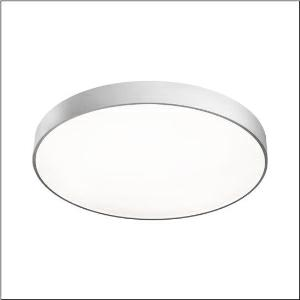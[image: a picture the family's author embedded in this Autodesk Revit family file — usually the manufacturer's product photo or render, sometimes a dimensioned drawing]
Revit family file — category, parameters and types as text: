
# Revit family: round_21_l_51mr38fd0421s
name_source: partatom
category: Lighting Fixtures
units: mm (PartAtom-declared; Revit-internal decimal feet)

## family parameters
Cut with Voids When Loaded = No
Host = Face
Light Source = No
Part Type = Normal
Room Calculation Point = No
Round Connector Dimension = Use Diameter
Shared = No

## types (1)
- Round 21 L (1 x LED, 13080 lm, 98.3 W, 4000K)
    Apparent Load = 98 VA
    CIE Flux Codes = 49 80 96 100 100
    Color Rendering = 80
    Color Temperature = 4000K
    Default Elevation = 1800 mm
    Description = Round 21 L, wall and ceiling luminaire, primary optical cover: cover, of PMMA, opal, light emission: direct distribution, primary light characteristic: symmetric, installation type: suspended mounting, surface-mounted, LED, rated luminous flux: 13.080lm, luminous efficacy: 133lm/W, light colour: 840, colour temperature: 4000K, with terminal, 5-pole, mains connection: 230V, AC, 50/60Hz, rated input power: 98W, housing, of aluminium, coated, silver, diameter: 850mm, height: 62mm, protection rating (complete): IP40, insulation class (complete): insulation class I (protective earthing), certification: CE, impact resistance: IK04, permissible operating ambient temperature: -10..+35°C, packaging unit: 1 piece
    Height = 87 mm
    Lamp = 1 x LED
    Lamp Light Flux = 13080 lm
    Lamp Power = 98.3 W
    Lamp count = 1
    Length = 850 mm
    Luminous efficacy = 133 lm/W
    Manufacturer = Siteco
    ModVariant = No
    Model = 51MR38FD0421S
    Mounting Place = Ceiling
    Mounting Type = Surface mounted
    Number of Poles = 1
    OnlyDefault = Yes
    Power Factor = 1
    Product Name = Round 21 L
    Product group = wall and ceiling luminaire
    ProductGroupID = 302
    Protection Class = Protection class I
    Protection Degree = IP 40
    RLX_Detail_Level = 1
    RLX_Emergency_Light_Flux = 0 lm
    RLX_Emergency_Type = 0
    RLX_Emergency_Type_DB = No
    RlxData = <blob elided: 20205 chars, md5=de1d65be>
    Socket = socket
    Standby Power = 0 W
    System Light Flux = 13080 lm
    System Power = 98 W
    Type Comments = Product without accessories
    Type Image = l_1258324.jpg
    URL = http://relux.com
    VarID = ---
    Voltage = 0 V
    Weight = 0.00 kg
    Width = 0 mm  [stored 0 ft]

note: [stored X ft] marks values corroborated as IEEE doubles in the binary element streams (Revit-internal decimal feet)

## geometry (parser evidence)
native form markers: Blend x4, Sweep x12
no freeform markers — native parametric forms only
